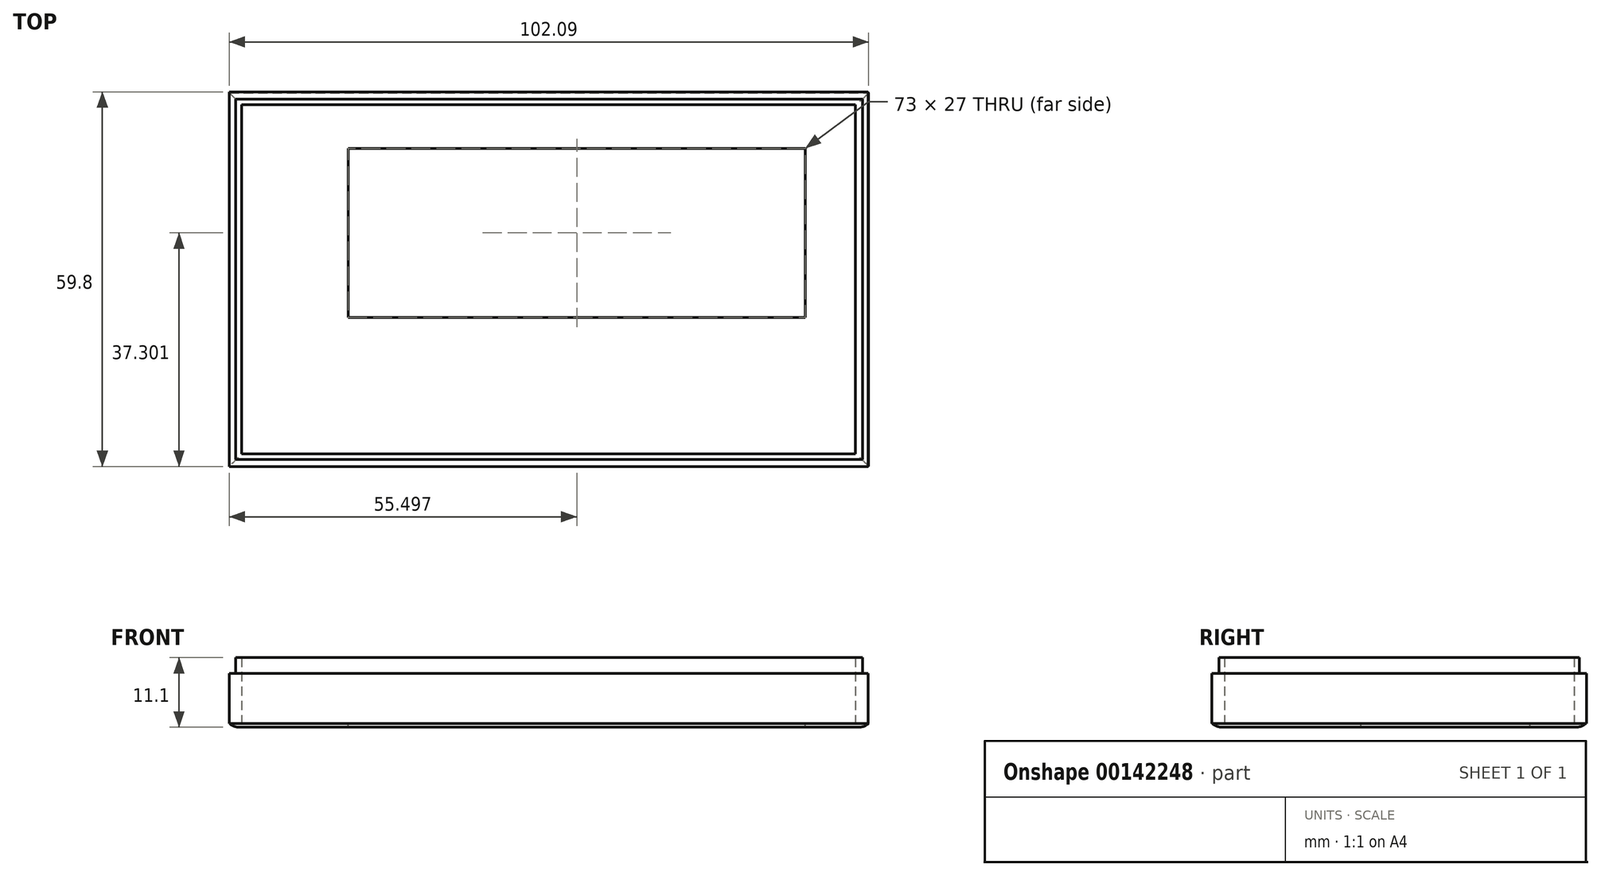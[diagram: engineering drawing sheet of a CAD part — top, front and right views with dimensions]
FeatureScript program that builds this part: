
annotation { "Feature Type Name" : "Feature", "Feature Type Description" : "" }
export const myFeature = defineFeature(function(context is Context, id is Id, definition is map)
    precondition{}
    {
        {
            var Q0;
            Q0=qCreatedBy(makeId("Top.planeOp"),FACE);
            var sketch = newSketch(context, id + "F0", { "sketchPlane" : qUnion([Q0])});
            skLineSegment(sketch, "E0.bottom", {"start": v(-62.16, 28.55) * mm, "end": v(39.84, 28.55) * mm});
            skLineSegment(sketch, "E0.top", {"start": v(-62.16, -31.25) * mm, "end": v(39.84, -31.25) * mm});
            skLineSegment(sketch, "E0.left", {"start": v(-62.16, 28.55) * mm, "end": v(-62.16, -31.25) * mm});
            skLineSegment(sketch, "E0.right", {"start": v(39.84, 28.55) * mm, "end": v(39.84, -31.25) * mm});
            skLineSegment(sketch, "E1.bottom", {"start": v(-60.16, 26.55) * mm, "end": v(37.84, 26.55) * mm});
            skLineSegment(sketch, "E1.top", {"start": v(-60.16, -29.25) * mm, "end": v(37.84, -29.25) * mm});
            skLineSegment(sketch, "E1.left", {"start": v(-60.16, 26.55) * mm, "end": v(-60.16, -29.25) * mm});
            skLineSegment(sketch, "E1.right", {"start": v(37.84, 26.55) * mm, "end": v(37.84, -29.25) * mm});
            skSolve(sketch);
        }
        {
            var Q0;
            Q0=qSketchRegion(id+"F0",true);
            extrude(context, id + "F1", {"entities" : qUnion([Q0]), "depth" : 8 * mm});
        }
        {
            var Q0;
            Q0=qCreatedBy(makeId("Top.planeOp"),FACE);
            var sketch = newSketch(context, id + "F2", { "sketchPlane" : qUnion([Q0])});
            skLineSegment(sketch, "E2.bottom", {"start": v(-62.13, -31.22) * mm, "end": v(39.93, -31.22) * mm});
            skLineSegment(sketch, "E2.top", {"start": v(-62.13, 28.45) * mm, "end": v(39.93, 28.45) * mm});
            skLineSegment(sketch, "E2.left", {"start": v(-62.13, -31.22) * mm, "end": v(-62.13, 28.45) * mm});
            skLineSegment(sketch, "E2.right", {"start": v(39.93, -31.22) * mm, "end": v(39.93, 28.45) * mm});
            skSolve(sketch);
        }
        {
            var Q0;
            Q0=makeQuery(id+"F2.imprint","IMPRINT",FACE,{"disambiguationData":[TD([[makeQuery(id+"F2.imprint","IMPRINT",EDGE,{"derivedFrom":sQuery(id+"F2.wireOp",EDGE,"E2.bottom")}),1.0]])]});
            var Q1;
            Q1=sQuery(id+"F2.wireOp",EDGE,"E2.left");
            var Q2;
            Q2=sQuery(id+"F2.wireOp",EDGE,"E2.bottom");
            var Q3;
            Q3=sQuery(id+"F2.wireOp",EDGE,"E2.top");
            var Q4;
            Q4=sQuery(id+"F2.wireOp",EDGE,"E2.right");
            extrude(context, id + "F3", {"entities" : qUnion([Q0]), "operationType" : NewBodyOperationType.ADD, "surfaceEntities" : qUnion([Q1, Q2, Q3, Q4]), "oppositeDirection" : true, "depth" : .6 * mm});
        }
        {
            var Q0;
            Q0=makeQuery(id+"F1.opExtrude","CAP_FACE",FACE,{"disambiguationData":[OSD([sQuery(id+"F0.wireOp",EDGE,"E0.bottom"),sQuery(id+"F0.wireOp",EDGE,"E0.top"),sQuery(id+"F0.wireOp",EDGE,"E0.left"),sQuery(id+"F0.wireOp",EDGE,"E0.right"),sQuery(id+"F0.wireOp",EDGE,"E1.bottom"),sQuery(id+"F0.wireOp",EDGE,"E1.top"),sQuery(id+"F0.wireOp",EDGE,"E1.left"),sQuery(id+"F0.wireOp",EDGE,"E1.right")])],"isStart":false});
            var sketch = newSketch(context, id + "F4", { "sketchPlane" : qUnion([Q0])});
            skLineSegment(sketch, "E3.bottom", {"start": v(-61.13, 27.42) * mm, "end": v(38.97, 27.42) * mm});
            skLineSegment(sketch, "E3.top", {"start": v(-61.13, -30.13) * mm, "end": v(38.97, -30.13) * mm});
            skLineSegment(sketch, "E3.left", {"start": v(-61.13, 27.42) * mm, "end": v(-61.13, -30.13) * mm});
            skLineSegment(sketch, "E3.right", {"start": v(38.97, 27.42) * mm, "end": v(38.97, -30.13) * mm});
            skSolve(sketch);
        }
        {
            var Q0;
            Q0=makeQuery(id+"F4.imprint","IMPRINT",FACE,{"disambiguationData":[TD([[makeQuery(id+"F4.imprint","IMPRINT",EDGE,{"derivedFrom":sQuery(id+"F4.wireOp",EDGE,"E3.bottom")}),-1.0]])]});
            extrude(context, id + "F5", {"entities" : qUnion([Q0]), "operationType" : NewBodyOperationType.ADD, "depth" : 2.5 * mm});
        }
        {
            var Q0;
            Q0=makeQuery(id+"F3.opExtrude","CAP_EDGE",EDGE,{"disambiguationData":[OSD([sQuery(id+"F2.wireOp",EDGE,"E2.bottom")])],"isStart":false});
            var Q1;
            Q1=makeQuery(id+"F3.opExtrude","CAP_EDGE",EDGE,{"disambiguationData":[OSD([sQuery(id+"F2.wireOp",EDGE,"E2.left")])],"isStart":false});
            var Q2;
            Q2=makeQuery(id+"F3.opExtrude","CAP_EDGE",EDGE,{"disambiguationData":[OSD([sQuery(id+"F2.wireOp",EDGE,"E2.right")])],"isStart":false});
            var Q3;
            Q3=makeQuery(id+"F3.opExtrude","CAP_EDGE",EDGE,{"disambiguationData":[OSD([sQuery(id+"F2.wireOp",EDGE,"E2.top")])],"isStart":false});
            fillet(context, id + "F6", {"entities" : qUnion([Q0, Q1, Q2, Q3]), "radius" : 2 * mm, "tangentPropagation" : true, "allowEdgeOverflow" : false});
        }
        {
            var Q0;
            Q0=makeQuery(id+"F4.imprint","IMPRINT",FACE,{"disambiguationData":[TD([[makeQuery(id+"F4.imprint","IMPRINT",EDGE,{"derivedFrom":makeQuery(id+"F1.opExtrude","CAP_EDGE",EDGE,{"disambiguationData":[OSD([sQuery(id+"F0.wireOp",EDGE,"E1.bottom")])],"isStart":false})}),-1.0]])]});
            var sketch = newSketch(context, id + "F7", { "sketchPlane" : qUnion([Q0])});
            skLineSegment(sketch, "E4.bottom", {"start": v(-43.16, 19.55) * mm, "end": v(29.84, 19.55) * mm});
            skLineSegment(sketch, "E4.top", {"start": v(-43.16, -7.45) * mm, "end": v(29.84, -7.45) * mm});
            skLineSegment(sketch, "E4.left", {"start": v(-43.16, 19.55) * mm, "end": v(-43.16, -7.45) * mm});
            skLineSegment(sketch, "E4.right", {"start": v(29.84, 19.55) * mm, "end": v(29.84, -7.45) * mm});
            skSolve(sketch);
        }
        {
            var Q0;
            Q0 = qSketchRegion(id + "F7", true);
            extrude(context, id + "F8", {"entities" : qUnion([Q0]), "operationType" : NewBodyOperationType.REMOVE, "endBound" : BoundingType.THROUGH_ALL, "oppositeDirection" : true, "depth" : 25 * mm});
        }
    });
